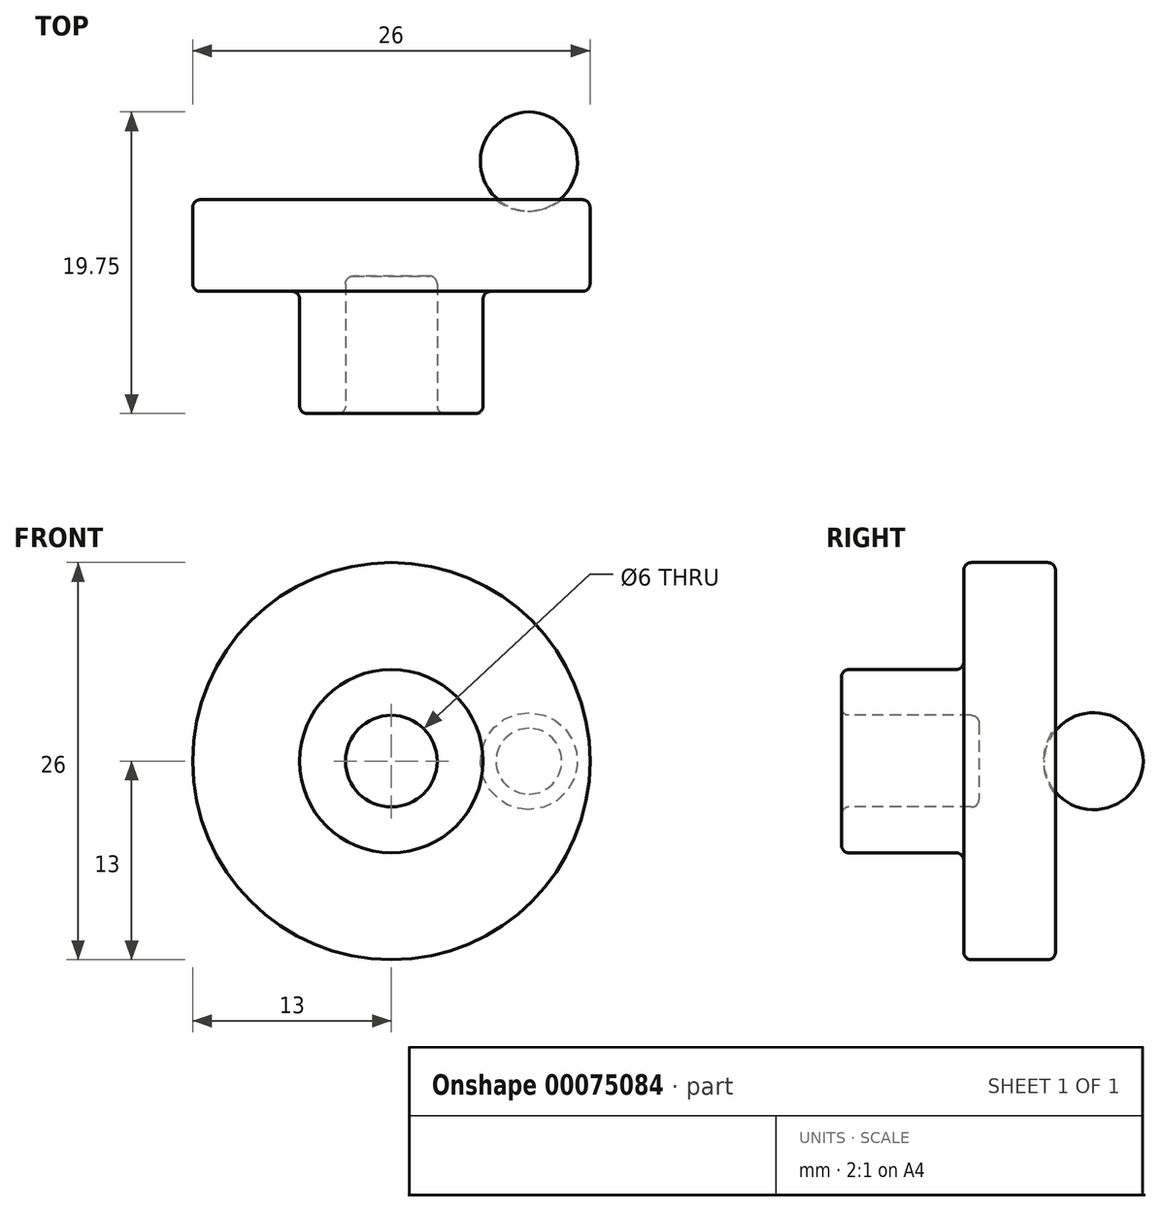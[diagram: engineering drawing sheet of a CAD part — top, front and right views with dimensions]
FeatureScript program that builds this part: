
annotation { "Feature Type Name" : "Feature", "Feature Type Description" : "" }
export const myFeature = defineFeature(function(context is Context, id is Id, definition is map)
    precondition{}
    {
        {
            var Q0;
            Q0=qCreatedBy(makeId("Top.planeOp"),FACE);
            var sketch = newSketch(context, id + "F0", { "sketchPlane" : qUnion([Q0])});
            skLineSegment(sketch, "E0", {"start": v(0, -12.16) * mm, "end": v(0, 14) * mm, "construction": true});
            skLineSegment(sketch, "E1", {"start": v(0, 14) * mm, "end": v(13, 14) * mm});
            skLineSegment(sketch, "E2", {"start": v(13, 14) * mm, "end": v(13, 8) * mm});
            skLineSegment(sketch, "E3", {"start": v(13, 8) * mm, "end": v(6, 8) * mm});
            skLineSegment(sketch, "E4", {"start": v(6, 8) * mm, "end": v(6, 0) * mm});
            skLineSegment(sketch, "E5", {"start": v(6, 0) * mm, "end": v(3, 0) * mm});
            skLineSegment(sketch, "E6", {"start": v(3, 0) * mm, "end": v(3, 9) * mm});
            skLineSegment(sketch, "E7", {"start": v(3, 9) * mm, "end": v(0, 9) * mm});
            skLineSegment(sketch, "E8", {"start": v(0, 9) * mm, "end": v(0, 14) * mm});
            skSolve(sketch);
        }
        {
            var Q0;
            Q0 = qSketchRegion(id + "F0", true);
            var Q1;
            Q1=sQuery(id+"F0.wireOp",EDGE,"E0");
            revolve(context, id + "F1", {"entities" : qUnion([Q0]), "axis" : qUnion([Q1]), "revolveType" : RevolveType.FULL});
        }
        {
            var Q0;
            Q0=makeQuery(id+"F1.opRevolve","SWEPT_EDGE",EDGE,{"disambiguationData":[OSD([sQuery(id+"F0.wireOp",EDGE,"E1"),sQuery(id+"F0.wireOp",EDGE,"E2")])]});
            var Q1;
            Q1=makeQuery(id+"F1.opRevolve","SWEPT_EDGE",EDGE,{"disambiguationData":[OSD([sQuery(id+"F0.wireOp",EDGE,"E2"),sQuery(id+"F0.wireOp",EDGE,"E3")])]});
            var Q2;
            Q2=makeQuery(id+"F1.opRevolve","SWEPT_FACE",FACE,{"disambiguationData":[OSD([sQuery(id+"F0.wireOp",EDGE,"E4")])]});
            var Q3;
            Q3=makeQuery(id+"F1.opRevolve","SWEPT_FACE",FACE,{"disambiguationData":[OSD([sQuery(id+"F0.wireOp",EDGE,"E6")])]});
            fillet(context, id + "F2", {"entities" : qUnion([Q0, Q1, Q2, Q3]), "radius" : .5 * mm, "tangentPropagation" : true, "allowEdgeOverflow" : false});
        }
        {
            var Q0;
            Q0=qCreatedBy(makeId("Top.planeOp"),FACE);
            var sketch = newSketch(context, id + "F3", { "sketchPlane" : qUnion([Q0])});
            skLineSegment(sketch, "E9.0.0", {"start": v(-12.5, 14) * mm, "end": v(12.5, 14) * mm, "construction": true});
            skLineSegment(sketch, "E10", {"start": v(-13, 8.5) * mm, "end": v(-13, 13.5) * mm, "construction": true});
            skLineSegment(sketch, "E11", {"start": v(13, 13.5) * mm, "end": v(13, 8.5) * mm, "construction": true});
            skLineSegment(sketch, "E12", {"start": v(9, 10.51) * mm, "end": v(9, 22.83) * mm, "construction": true});
            skLineSegment(sketch, "E13", {"start": v(6.65, 16.5) * mm, "end": v(11.5, 16.5) * mm, "construction": true});
            skArc(sketch, "E14", {"start": v(9, 13.25) * mm, "mid": v(12.32, 16.5) * mm, "end": v(9, 19.75) * mm});
            skLineSegment(sketch, "E15", {"start": v(9, 13.25) * mm, "end": v(9, 19.75) * mm});
            skSolve(sketch);
        }
        {
            var Q0;
            Q0 = qSketchRegion(id + "F3", true);
            var Q1;
            Q1=sQuery(id+"F3.wireOp",EDGE,"E15");
            revolve(context, id + "F4", {"operationType" : NewBodyOperationType.REMOVE, "entities" : qUnion([Q0]), "axis" : qUnion([Q1]), "revolveType" : RevolveType.FULL, "oppositeDirection" : true});
        }
    });
